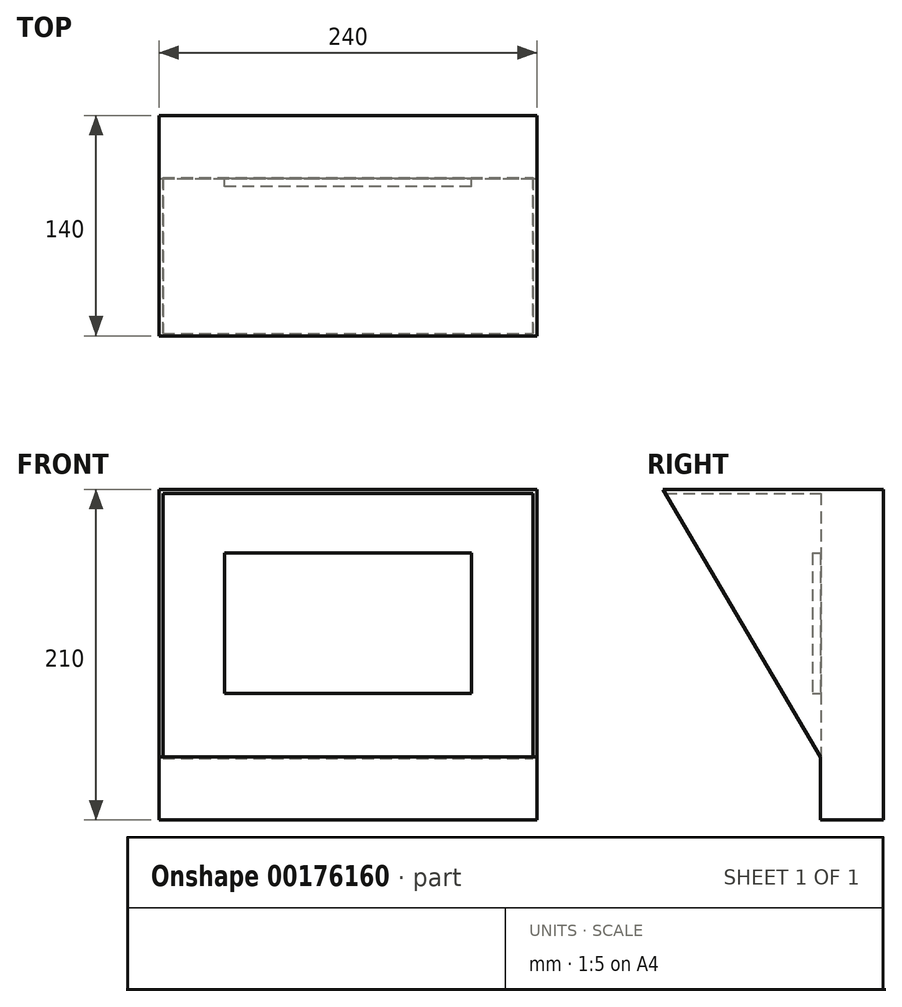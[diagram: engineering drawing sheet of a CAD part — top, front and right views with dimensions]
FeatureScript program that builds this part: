
annotation { "Feature Type Name" : "Feature", "Feature Type Description" : "" }
export const myFeature = defineFeature(function(context is Context, id is Id, definition is map)
    precondition{}
    {
        {
            var Q0;
            Q0=qCreatedBy(makeId("Front.planeOp"),FACE);
            var sketch = newSketch(context, id + "F0", { "sketchPlane" : qUnion([Q0])});
            skLineSegment(sketch, "E0.bottom", {"start": v(120, 85) * mm, "end": v(-120, 85) * mm});
            skLineSegment(sketch, "E0.top", {"start": v(120, -85) * mm, "end": v(-120, -85) * mm});
            skLineSegment(sketch, "E0.left", {"start": v(120, 85) * mm, "end": v(120, -85) * mm});
            skLineSegment(sketch, "E0.right", {"start": v(-120, 85) * mm, "end": v(-120, -85) * mm});
            skPoint(sketch, "E0.middle", {"position": v(0, 0) * mm});
            skLineSegment(sketch, "E1.bottom", {"start": v(78.45, 44.5) * mm, "end": v(-78.45, 44.5) * mm});
            skLineSegment(sketch, "E1.top", {"start": v(78.45, -44.5) * mm, "end": v(-78.45, -44.5) * mm});
            skLineSegment(sketch, "E1.left", {"start": v(78.45, 44.5) * mm, "end": v(78.45, -44.5) * mm});
            skLineSegment(sketch, "E1.right", {"start": v(-78.45, 44.5) * mm, "end": v(-78.45, -44.5) * mm});
            skSolve(sketch);
        }
        {
            var Q0;
            Q0=qCreatedBy(makeId("Right.planeOp"),FACE);
            var sketch = newSketch(context, id + "F1", { "sketchPlane" : qUnion([Q0])});
            skLineSegment(sketch, "E2", {"start": v(0, 0) * mm, "end": v(0, 85) * mm});
            skLineSegment(sketch, "E3", {"start": v(0, 0) * mm, "end": v(0, -85) * mm});
            skLineSegment(sketch, "E4", {"start": v(0, 85) * mm, "end": v(100, 85) * mm});
            skLineSegment(sketch, "E5.bottom", {"start": v(0, 85) * mm, "end": v(-40, 85) * mm});
            skLineSegment(sketch, "E5.top", {"start": v(0, -85) * mm, "end": v(-40, -85) * mm});
            skLineSegment(sketch, "E5.left", {"start": v(0, 85) * mm, "end": v(0, -85) * mm});
            skLineSegment(sketch, "E5.right", {"start": v(-40, 85) * mm, "end": v(-40, -85) * mm});
            skLineSegment(sketch, "E6", {"start": v(0, -85) * mm, "end": v(100, 85) * mm});
            skLineSegment(sketch, "E7.left", {"start": v(0, -85) * mm, "end": v(0, -85) * mm});
            skLineSegment(sketch, "E7.right", {"start": v(-40, -85) * mm, "end": v(-40, -85) * mm});
            skLineSegment(sketch, "E8.top", {"start": v(0, -125) * mm, "end": v(-40, -125) * mm});
            skLineSegment(sketch, "E8.left", {"start": v(0, -85) * mm, "end": v(0, -125) * mm});
            skLineSegment(sketch, "E8.right", {"start": v(-40, -85) * mm, "end": v(-40, -125) * mm});
            skSolve(sketch);
        }
        {
            var Q0;
            Q0=makeQuery(id+"F1.imprint","IMPRINT",FACE,{"disambiguationData":[TD([[makeQuery(id+"F1.imprint","IMPRINT",EDGE,{"derivedFrom":sQuery(id+"F1.wireOp",EDGE,"E5.bottom")}),1.0]])]});
            extrude(context, id + "F2", {"entities" : qUnion([Q0]), "endBound" : BoundingType.SYMMETRIC, "depth" : 240 * mm, "offsetDistance" : 25 * mm});
        }
        {
            var Q0;
            Q0=makeQuery(id+"F1.imprint","IMPRINT",FACE,{"disambiguationData":[TD([[makeQuery(id+"F1.imprint","IMPRINT",EDGE,{"derivedFrom":sQuery(id+"F1.wireOp",EDGE,"E5.top")}),1.0]])]});
            extrude(context, id + "F3", {"entities" : qUnion([Q0]), "operationType" : NewBodyOperationType.ADD, "endBound" : BoundingType.SYMMETRIC, "depth" : 240 * mm, "offsetDistance" : 25 * mm});
        }
        {
            var Q0;
            Q0=makeQuery(id+"F1.imprint","IMPRINT",FACE,{"disambiguationData":[TD([[makeQuery(id+"F1.imprint","IMPRINT",EDGE,{"derivedFrom":sQuery(id+"F1.wireOp",EDGE,"E4")}),-1.0]])]});
            extrude(context, id + "F4", {"entities" : qUnion([Q0]), "operationType" : NewBodyOperationType.ADD, "endBound" : BoundingType.SYMMETRIC, "depth" : 240 * mm, "offsetDistance" : 25 * mm});
        }
        {
            var Q0;
            Q0=makeQuery(id+"F4.opExtrude","SWEPT_FACE",FACE,{"disambiguationData":[OSD([sQuery(id+"F1.wireOp",EDGE,"E6")])]});
            shell(context, id + "F5", {"entities" : qUnion([Q0]), "thickness" : 2.5 * mm});
        }
        {
            var Q0;
            Q0=makeQuery(id+"F0.imprint","IMPRINT",FACE,{"disambiguationData":[TD([[makeQuery(id+"F0.imprint","IMPRINT",EDGE,{"derivedFrom":sQuery(id+"F0.wireOp",EDGE,"E1.bottom")}),1.0]])]});
            extrude(context, id + "F6", {"entities" : qUnion([Q0]), "depth" : 5 * mm, "offsetDistance" : 25 * mm});
        }
        {
            var Q0;
            Q0=makeQuery(id+"F2.opExtrude","SWEPT_BODY",BODY,{"disambiguationData":[OSD([sQuery(id+"F1.wireOp",EDGE,"E5.bottom"),sQuery(id+"F1.wireOp",EDGE,"E5.left"),sQuery(id+"F1.wireOp",EDGE,"E5.right"),sQuery(id+"F1.wireOp",EDGE,"E5.top")])]});
            var Q1;
            Q1=sQuery(id+"F1.wireOp",EDGE,"E5.left");
            transform(context, id + "F7", {"entities" : qUnion([Q0]), "transformType" : TransformType.ROTATION, "transformAxis" : qUnion([Q1]), "angle" : 180 * degree, "makeCopy" : false});
        }
        {
            var Q0;
            Q0=makeQuery(id+"F5.opShell","OFFSET_FACE",FACE,{"disambiguationData":[OSD([sQuery(id+"F1.wireOp",EDGE,"E5.right"),sQuery(id+"F1.wireOp",EDGE,"E8.right")])]});
            extrude(context, id + "F8", {"entities" : qUnion([Q0]), "operationType" : NewBodyOperationType.ADD, "depth" : 37 * mm, "offsetDistance" : 25 * mm});
        }
    });
